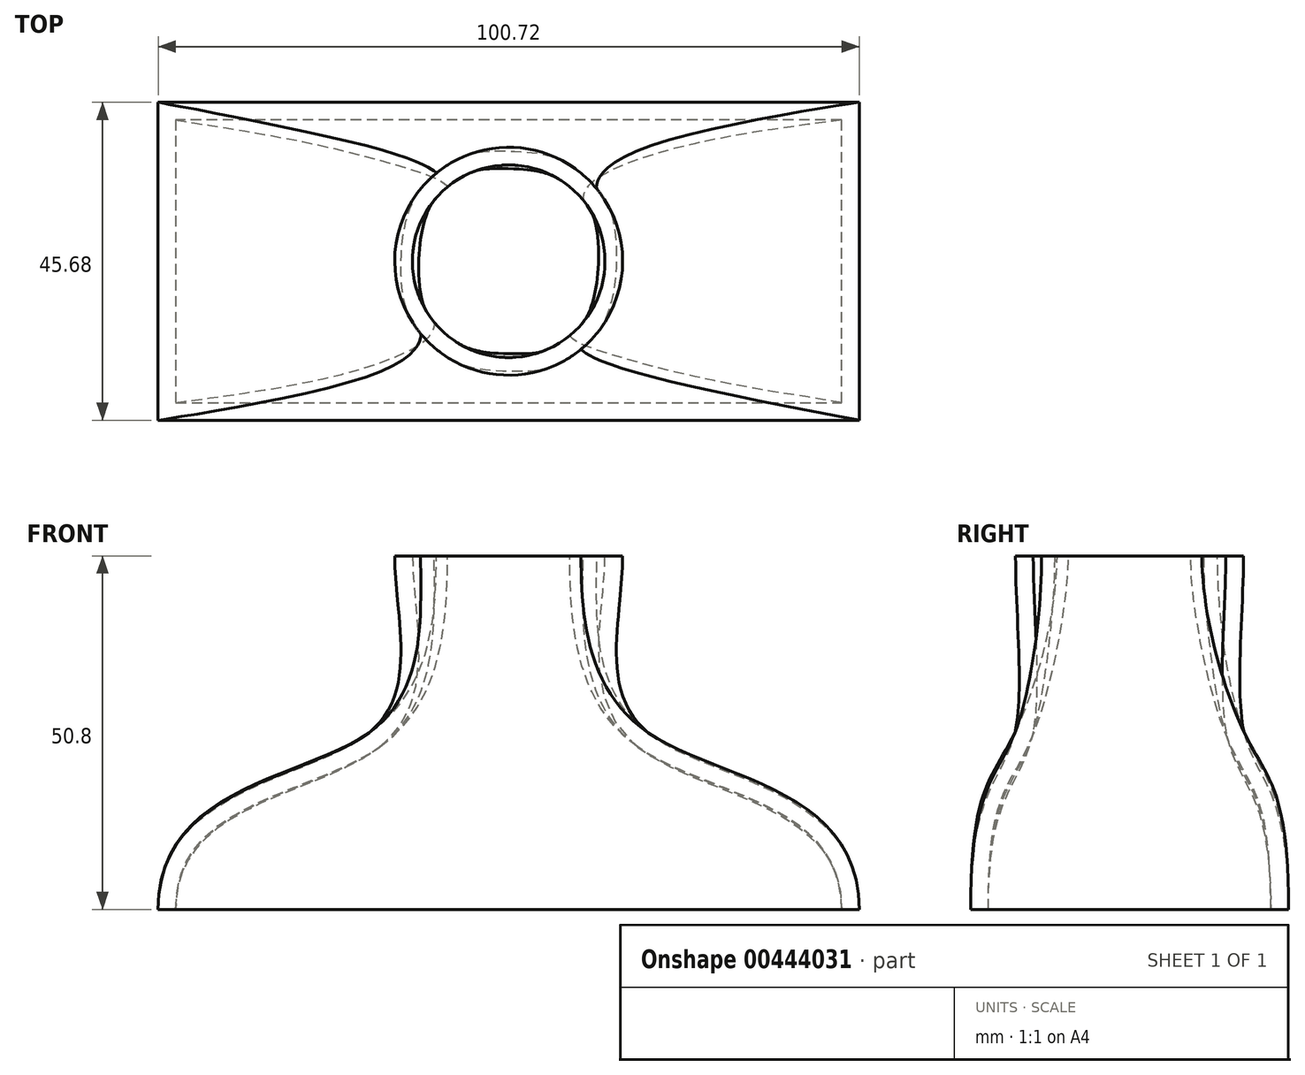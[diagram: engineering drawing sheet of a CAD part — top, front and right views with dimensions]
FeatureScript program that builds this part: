
annotation { "Feature Type Name" : "Feature", "Feature Type Description" : "" }
export const myFeature = defineFeature(function(context is Context, id is Id, definition is map)
    precondition{}
    {
        {
            var Q0;
            Q0=qCreatedBy(makeId("Top.planeOp"),FACE);
            var sketch = newSketch(context, id + "F0", { "sketchPlane" : qUnion([Q0])});
            skLineSegment(sketch, "E0.bottom", {"start": v(50.36, 22.84) * mm, "end": v(-50.36, 22.84) * mm});
            skLineSegment(sketch, "E0.top", {"start": v(50.36, -22.84) * mm, "end": v(-50.36, -22.84) * mm});
            skLineSegment(sketch, "E0.left", {"start": v(50.36, 22.84) * mm, "end": v(50.36, -22.84) * mm});
            skLineSegment(sketch, "E0.right", {"start": v(-50.36, 22.84) * mm, "end": v(-50.36, -22.84) * mm});
            skPoint(sketch, "E0.middle", {"position": v(0, 0) * mm});
            skSolve(sketch);
        }
        {
            var Q0;
            Q0=qCreatedBy(makeId("Top.planeOp"),FACE);
            cPlane(context, id + "F1", {"entities" : qUnion([Q0]), "cplaneType" : CPlaneType.OFFSET, "offset" : 25.4 * mm, "width" : 152.4 * mm, "height" : 152.4 * mm});
        }
        {
            var Q0;
            Q0=qCreatedBy(makeId("Top.planeOp"),FACE);
            cPlane(context, id + "F2", {"entities" : qUnion([Q0]), "cplaneType" : CPlaneType.OFFSET, "offset" : 50.8 * mm, "width" : 152.4 * mm, "height" : 152.4 * mm});
        }
        {
            var Q0;
            Q0=qCreatedBy(id+"F1.planeOp",FACE);
            var sketch = newSketch(context, id + "F3", { "sketchPlane" : qUnion([Q0])});
            skLineSegment(sketch, "E1.bottom", {"start": v(20.03, 16.48) * mm, "end": v(-20.03, 16.48) * mm});
            skLineSegment(sketch, "E1.top", {"start": v(20.03, -16.48) * mm, "end": v(-20.03, -16.48) * mm});
            skLineSegment(sketch, "E1.left", {"start": v(20.03, 16.48) * mm, "end": v(20.03, -16.48) * mm});
            skLineSegment(sketch, "E1.right", {"start": v(-20.03, 16.48) * mm, "end": v(-20.03, -16.48) * mm});
            skPoint(sketch, "E1.middle", {"position": v(0, 0) * mm});
            skSolve(sketch);
        }
        {
            var Q0;
            Q0=qCreatedBy(id+"F2.planeOp",FACE);
            var sketch = newSketch(context, id + "F4", { "sketchPlane" : qUnion([Q0])});
            skCircle(sketch, "E2", {"center": v(0, 0) * mm, "radius": 16.37 * mm});
            skSolve(sketch);
        }
        {
            var Q0;
            Q0=makeQuery(id+"F0.imprint","IMPRINT",FACE,{"disambiguationData":[TD([[makeQuery(id+"F0.imprint","IMPRINT",EDGE,{"derivedFrom":sQuery(id+"F0.wireOp",EDGE,"E0.bottom")}),1.0]])]});
            var Q1;
            Q1=makeQuery(id+"F3.imprint","IMPRINT",FACE,{"disambiguationData":[TD([[makeQuery(id+"F3.imprint","IMPRINT",EDGE,{"derivedFrom":sQuery(id+"F3.wireOp",EDGE,"E1.bottom")}),1.0]])]});
            var Q2;
            Q2=makeQuery(id+"F4.imprint","IMPRINT",FACE,{"disambiguationData":[TD([[makeQuery(id+"F4.imprint","IMPRINT",EDGE,{"derivedFrom":sQuery(id+"F4.wireOp",EDGE,"E2")}),1.0]])]});
            var Q3;
            Q3=makeQuery(id+"F4.imprint","IMPRINT",FACE,{"disambiguationData":[TD([[makeQuery(id+"F4.imprint","IMPRINT",EDGE,{"derivedFrom":sQuery(id+"F4.wireOp",EDGE,"E2")}),1.0]])]});
            var Q4;
            Q4=makeQuery(id+"F3.imprint","IMPRINT",FACE,{"disambiguationData":[TD([[makeQuery(id+"F3.imprint","IMPRINT",EDGE,{"derivedFrom":sQuery(id+"F3.wireOp",EDGE,"E1.bottom")}),1.0]])]});
            var Q5;
            Q5=makeQuery(id+"F0.imprint","IMPRINT",FACE,{"disambiguationData":[TD([[makeQuery(id+"F0.imprint","IMPRINT",EDGE,{"derivedFrom":sQuery(id+"F0.wireOp",EDGE,"E0.bottom")}),1.0]])]});
            loft(context, id + "F5", {"startCondition" : LoftEndDerivativeType.NORMAL_TO_PROFILE, "startMagnitude" : 2, "endCondition" : LoftEndDerivativeType.NORMAL_TO_PROFILE, "endMagnitude" : 1, "sheetProfilesArray" : [{ "sheetProfileEntities" : qUnion([Q0]) }, { "sheetProfileEntities" : qUnion([Q1]) }, { "sheetProfileEntities" : qUnion([Q2]) }], "wireProfilesArray" : [{ "wireProfileEntities" : qUnion([Q3]) }, { "wireProfileEntities" : qUnion([Q4]) }, { "wireProfileEntities" : qUnion([Q5]) }]});
        }
        {
            var Q0;
            Q0=makeQuery(id+"F5.opLoft","CAP_FACE",FACE,{"disambiguationData":[OSD([makeQuery(id+"F0.imprint","IMPRINT",FACE,{"disambiguationData":[TD([[makeQuery(id+"F0.imprint","IMPRINT",EDGE,{"derivedFrom":sQuery(id+"F0.wireOp",EDGE,"E0.bottom")}),1.0]])]})])],"isStart":true});
            var Q1;
            Q1=makeQuery(id+"F5.opLoft","CAP_FACE",FACE,{"disambiguationData":[OSD([makeQuery(id+"F4.imprint","IMPRINT",FACE,{"disambiguationData":[TD([[makeQuery(id+"F4.imprint","IMPRINT",EDGE,{"derivedFrom":sQuery(id+"F4.wireOp",EDGE,"E2")}),1.0]])]})])],"isStart":true});
            shell(context, id + "F6", {"entities" : qUnion([Q0, Q1]), "thickness" : 2.54 * mm});
        }
    });
